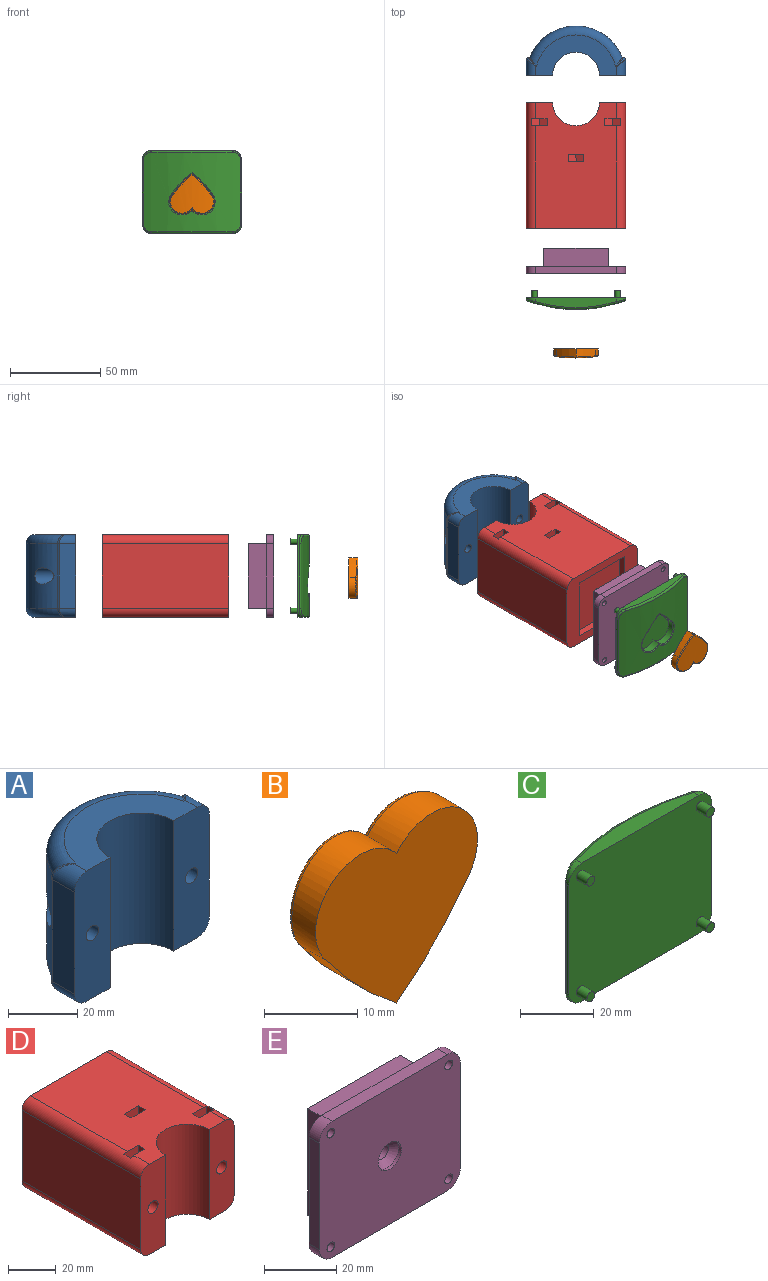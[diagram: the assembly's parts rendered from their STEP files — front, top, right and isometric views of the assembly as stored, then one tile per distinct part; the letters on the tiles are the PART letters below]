
ASSEMBLY  parts=5 mates=4
PART A: 32 faces, bbox 58x29.8x46 mm
  f0: cylinder r=27.5mm len=51.23mm, axis (0,0,-1), area 2176.9mm2, adj f4,f5,f10,f11,f18,f23
  f1: cylinder r=13mm len=46mm, axis (0,0,-1), area 1878.7mm2, adj f2,f7,f8,f9
  f2: plane 46x14.5mm, normal (0,-1,0), area 636.6mm2, adj f1,f3,f8,f9,f14,f16,f21
  f3: plane 36x9mm, normal (1,0,0), area 324mm2, adj f2,f16,f21,f27
  f4: plane 36x0.88mm, normal (0,1,0), area 31.8mm2, adj f0,f17,f22,f27
  f5: plane 36x0.88mm, normal (0,1,0), area 31.8mm2, adj f0,f19,f24,f30
  f6: plane 36x9mm, normal (-1,0,0), area 324mm2, adj f7,f20,f25,f30
  f7: plane 46x14.5mm, normal (0,-1,0), area 636.6mm2, adj f1,f6,f8,f9,f12,f20,f25
  f8: plane 45x22.5mm, normal (0,0,1), area 531.6mm2, adj f1,f2,f7,f21,f22,f23,f24,f25
  f9: plane 45x22.5mm, normal (0,0,-1), area 531.6mm2, adj f1,f2,f7,f16,f17,f18,f19,f20
  f10: cylinder r=4.5mm len=17.54mm, axis (0,-1,0), area 366.3mm2, adj f0,f15
  f11: cylinder r=4.5mm len=17.54mm, axis (0,-1,0), area 366.3mm2, adj f0,f13
  f12: cylinder r=2.5mm len=5mm, axis (0,1,0), area 78.5mm2, adj f7,f13
  f13: plane 9x9mm, normal (0,1,0), area 44mm2, adj f11,f12
  f14: cylinder r=2.5mm len=5mm, axis (0,1,0), area 78.5mm2, adj f2,f15
  f15: plane 9x9mm, normal (0,1,0), area 44mm2, adj f10,f14
  f16: cylinder r=5mm len=9mm, axis (0,1,0), area 59.3mm2, adj f2,f3,f9,f26
  f17: cylinder r=5mm len=5mm, axis (-1,0,0), area 5.7mm2, adj f4,f9,f18,f26
  f18: torus R=22.5mm, axis (0,0,1), area 502.8mm2, adj f0,f9,f17,f19
  f19: cylinder r=5mm len=5mm, axis (-1,0,0), area 5.7mm2, adj f5,f9,f18,f29
  f20: cylinder r=5mm len=9mm, axis (0,-1,0), area 59.3mm2, adj f6,f7,f9,f29
  f21: cylinder r=5mm len=9mm, axis (0,-1,0), area 59.3mm2, adj f2,f3,f8,f28
  f22: cylinder r=5mm len=5mm, axis (1,0,0), area 5.7mm2, adj f4,f8,f23,f28
  f23: torus R=22.5mm, axis (0,0,1), area 502.8mm2, adj f0,f8,f22,f24
  f24: cylinder r=5mm len=5mm, axis (1,0,0), area 5.7mm2, adj f5,f8,f23,f31
  f25: cylinder r=5mm len=9mm, axis (0,1,0), area 59.3mm2, adj f6,f7,f8,f31
  f26: bspline ~5.78x5mm, area 8.5mm2, adj f16,f17,f27
  f27: cylinder r=1mm len=36mm, axis (0,0,-1), area 56.5mm2, adj f3,f4,f26,f28
  f28: bspline ~5.78x5mm, area 8.5mm2, adj f21,f22,f27
  f29: bspline ~5.78x5mm, area 8.5mm2, adj f19,f20,f30
  f30: cylinder r=1mm len=36mm, axis (0,0,-1), area 56.5mm2, adj f5,f6,f29,f31
  f31: bspline ~5.78x5mm, area 8.5mm2, adj f24,f25,f30
PART B: 10 faces, bbox 24.7x5x23.2 mm
  f0: cylinder r=6.89mm len=12.32mm, axis (0,-1,0), area 91.1mm2, adj f1,f3,f4,f9
  f1: cylinder r=6.89mm len=12.32mm, axis (0,-1,0), area 91.1mm2, adj f0,f2,f4,f8
  f2: cylinder r=51.6mm len=10.96mm, axis (0,-1,0), area 65.5mm2, adj f1,f3,f4,f6,f8
  f3: cylinder r=51.6mm len=10.96mm, axis (0,-1,0), area 65.5mm2, adj f0,f2,f4,f7,f9
  f4: plane 24.64x22.3mm, normal (0,-1,0), area 374.5mm2, adj f0,f1,f2,f3
  f5: cylinder r=78.12mm len=23.79mm, axis (0,0,-1), area 330.5mm2, adj f6,f7,f8,f9
  f6: bspline ~14.11x13.57mm, area 11.5mm2, adj f2,f5,f7,f8
  f7: bspline ~14.11x13.57mm, area 11.5mm2, adj f3,f5,f6,f9
  f8: bspline ~13.21x11.89mm, area 16.3mm2, adj f1,f2,f5,f6,f9
  f9: bspline ~13.33x12.41mm, area 16.3mm2, adj f0,f3,f5,f7,f8
PART C: 35 faces, bbox 55x16.9x46 mm
  f0: plane 55x46mm, normal (0,-1,0), area 2480.3mm2, adj f1,f3,f4,f5,f6,f8,f10,f12
  f1: plane 36x0.8mm, normal (1,0,0), area 29mm2, adj f0,f19,f21,f25
  f2: cylinder r=78.12mm len=53.69mm, axis (0,0,-1), area 1973.2mm2, adj f23,f24,f25,f26,f27,f28,f29,f30
  f3: plane 36x0.8mm, normal (-1,0,0), area 29mm2, adj f0,f20,f22,f28
  f4: plane 45x5.5mm, normal (0,0,1), area 197.6mm2, adj f0,f21,f22,f29
  f5: plane 45x5.5mm, normal (0,0,-1), area 197.6mm2, adj f0,f19,f20,f24
  f6: cylinder r=1.5mm len=4mm, axis (0,1,0), area 37.7mm2, adj f0,f7
  f7: plane 3x3mm, normal (0,-1,0), area 7.1mm2, adj f6
  f8: cylinder r=1.5mm len=4mm, axis (0,1,0), area 37.7mm2, adj f0,f9
  f9: plane 3x3mm, normal (0,-1,0), area 7.1mm2, adj f8
  f10: cylinder r=1.5mm len=4mm, axis (0,1,0), area 37.7mm2, adj f0,f11
  f11: plane 3x3mm, normal (0,-1,0), area 7.1mm2, adj f10
  f12: cylinder r=1.5mm len=4mm, axis (0,1,0), area 37.7mm2, adj f0,f13
  f13: plane 3x3mm, normal (0,-1,0), area 7.1mm2, adj f12
  f14: cylinder r=6.89mm len=12.32mm, axis (0,-1,0), area 86mm2, adj f15,f17,f18,f32,f34
  f15: cylinder r=6.89mm len=12.32mm, axis (0,-1,0), area 86mm2, adj f14,f16,f18,f31,f33
  f16: cylinder r=51.6mm len=10.96mm, axis (0,-1,0), area 63mm2, adj f15,f17,f18,f31
  f17: cylinder r=51.6mm len=10.96mm, axis (0,-1,0), area 63mm2, adj f14,f16,f18,f32
  f18: plane 24.64x22.3mm, normal (0,1,0), area 374.5mm2, adj f14,f15,f16,f17
  f19: cylinder r=5mm len=5mm, axis (0,1,0), area 11.6mm2, adj f0,f1,f5,f23
  f20: cylinder r=5mm len=5mm, axis (0,-1,0), area 11.6mm2, adj f0,f3,f5,f26
  f21: cylinder r=5mm len=5mm, axis (0,-1,0), area 11.6mm2, adj f0,f1,f4,f27
  f22: cylinder r=5mm len=5mm, axis (0,1,0), area 11.6mm2, adj f0,f3,f4,f30
  f23: bspline ~6.14x6.08mm, area 10mm2, adj f2,f19,f24,f25
  f24: torus R=77.12mm, axis (0,0,1), area 72.3mm2, adj f2,f5,f23,f26
  f25: cylinder r=1mm len=36mm, axis (0,0,-1), area 43.9mm2, adj f1,f2,f23,f27
  f26: bspline ~6.14x5.29mm, area 10mm2, adj f2,f20,f24,f28
  f27: bspline ~6.14x5.29mm, area 10mm2, adj f2,f21,f25,f29
  f28: cylinder r=1mm len=36mm, axis (0,0,-1), area 43.9mm2, adj f2,f3,f26,f30
  f29: torus R=77.12mm, axis (0,0,1), area 72.3mm2, adj f2,f4,f27,f30
  f30: bspline ~6.14x6.08mm, area 10mm2, adj f2,f22,f28,f29
  f31: bspline ~17.03x16.48mm, area 12.7mm2, adj f2,f15,f16,f32,f33
  f32: bspline ~17.03x16.48mm, area 12.7mm2, adj f2,f14,f17,f31,f34
  f33: bspline ~13.85x13.31mm, area 18.3mm2, adj f2,f15,f31,f34
  f34: bspline ~13.65x12.76mm, area 18.3mm2, adj f2,f14,f32,f33
PART D: 64 faces, bbox 55x70x46 mm
  f0: cylinder r=3mm len=33mm, axis (0,1,0), area 622mm2, adj f31,f36
  f1: plane 55x46mm, normal (0,1,0), area 1212.5mm2, adj f2,f4,f5,f6,f27,f28,f29,f30
  f2: plane 70x45mm, normal (0,0,1), area 2798.5mm2, adj f1,f3,f7,f8,f11,f15,f16,f22
  f3: plane 46x14.5mm, normal (0,-1,0), area 628mm2, adj f2,f5,f6,f8,f10,f41,f42
  f4: plane 70x36mm, normal (-1,0,0), area 2520mm2, adj f1,f7,f40,f43
  f5: plane 70x45mm, normal (0,0,-1), area 2884.5mm2, adj f1,f3,f7,f8,f40,f41
  f6: plane 70x36mm, normal (1,0,0), area 2520mm2, adj f1,f3,f41,f42
  f7: plane 46x14.5mm, normal (0,-1,0), area 628mm2, adj f2,f4,f5,f8,f9,f40,f43
  f8: cylinder r=13mm len=46mm, axis (0,0,-1), area 1878.7mm2, adj f2,f3,f5,f7
  f9: cylinder r=3mm len=9mm, axis (0,-1,0), area 169.6mm2, adj f7,f24
  f10: cylinder r=3mm len=9mm, axis (0,-1,0), area 169.6mm2, adj f3,f16
  f11: plane 25.45x4mm, normal (1,0,0), area 101.8mm2, adj f2,f12,f15,f16
  f12: plane 4.25x4mm, normal (0.5,0,0.87), area 19.6mm2, adj f11,f13,f15,f16
  f13: plane 4.25x4mm, normal (-0.5,0,0.87), area 19.6mm2, adj f12,f14,f15,f16
  f14: plane 25.04x4mm, normal (-1,0,0), area 100.1mm2, adj f13,f15,f16,f42
  f15: plane 27.91x8.5mm, normal (0,-1,0), area 198.2mm2, adj f2,f11,f12,f13,f14,f18,f42
  f16: plane 27.91x8.5mm, normal (0,1,0), area 198.2mm2, adj f2,f10,f11,f12,f13,f14,f42
  f17: cone r=0mm half-angle=59deg, axis (0,-1,0), area 33mm2, adj f18
  f18: cylinder r=3mm len=6mm, axis (0,-1,0), area 37.7mm2, adj f15,f17
  f19: plane 25.04x4mm, normal (1,0,0), area 100.1mm2, adj f20,f23,f24,f43
  f20: plane 4.25x4mm, normal (0.5,0,0.87), area 19.6mm2, adj f19,f21,f23,f24
  f21: plane 4.25x4mm, normal (-0.5,0,0.87), area 19.6mm2, adj f20,f22,f23,f24
  f22: plane 25.45x4mm, normal (-1,0,0), area 101.8mm2, adj f2,f21,f23,f24
  f23: plane 27.91x8.5mm, normal (0,-1,0), area 198.2mm2, adj f2,f19,f20,f21,f22,f26,f43
  f24: plane 27.91x8.5mm, normal (0,1,0), area 198.2mm2, adj f2,f9,f19,f20,f21,f22,f43
  f25: cone r=0mm half-angle=59deg, axis (0,-1,0), area 33mm2, adj f26
  f26: cylinder r=3mm len=6mm, axis (0,-1,0), area 37.7mm2, adj f23,f25
  f27: plane 36x4mm, normal (0,0,1), area 144mm2, adj f1,f28,f30,f31
  f28: plane 36x4mm, normal (-1,0,0), area 144mm2, adj f1,f27,f29,f31
  f29: plane 36x4mm, normal (0,0,-1), area 144mm2, adj f1,f28,f30,f31
  f30: plane 36x4mm, normal (1,0,0), area 144mm2, adj f1,f27,f29,f31
  f31: plane 36x36mm, normal (0,1,0), area 1267.7mm2, adj f0,f27,f28,f29,f30
  f32: plane 25.45x4mm, normal (1,0,0), area 101.8mm2, adj f2,f33,f36,f37
  f33: plane 4.25x4mm, normal (0.5,0,0.87), area 19.6mm2, adj f32,f34,f36,f37
  f34: plane 4.25x4mm, normal (-0.5,0,0.87), area 19.6mm2, adj f33,f35,f36,f37
  f35: plane 25.45x4mm, normal (-1,0,0), area 101.8mm2, adj f2,f34,f36,f37
  f36: plane 27.91x8.5mm, normal (0,-1,0), area 198.5mm2, adj f0,f2,f32,f33,f34,f35
  f37: plane 27.91x8.5mm, normal (0,1,0), area 198.5mm2, adj f2,f32,f33,f34,f35,f39
  f38: cone r=0mm half-angle=59deg, axis (0,1,0), area 33mm2, adj f39
  f39: cylinder r=3mm len=6mm, axis (0,1,0), area 18.8mm2, adj f37,f38
  f40: cylinder r=5mm len=70mm, axis (0,-1,0), area 549.8mm2, adj f1,f4,f5,f7
  f41: cylinder r=5mm len=70mm, axis (0,1,0), area 549.8mm2, adj f1,f3,f5,f6
  f42: cylinder r=5mm len=70mm, axis (0,-1,0), area 541.5mm2, adj f1,f2,f3,f6,f14,f15,f16
  f43: cylinder r=5mm len=70mm, axis (0,1,0), area 541.5mm2, adj f1,f2,f4,f7,f19,f23,f24
  f44: plane 43x5.25mm, normal (0,0,1), area 225.7mm2, adj f45,f51,f52,f53
  f45: cylinder r=5mm len=43mm, axis (0,-1,0), area 337.7mm2, adj f44,f46,f52,f53
  f46: plane 43x28mm, normal (-1,0,0), area 1204mm2, adj f45,f47,f52,f53
  f47: cylinder r=5mm len=43mm, axis (0,-1,0), area 337.7mm2, adj f46,f48,f52,f53
  f48: plane 43x5.25mm, normal (0,0,-1), area 225.7mm2, adj f47,f49,f52,f53
  f49: cylinder r=5mm len=43mm, axis (0,-1,0), area 337.7mm2, adj f48,f50,f52,f53
  f50: plane 43x28mm, normal (1,0,0), area 1204mm2, adj f49,f51,f52,f53
  f51: cylinder r=5mm len=43mm, axis (0,-1,0), area 337.7mm2, adj f44,f50,f52,f53
  f52: plane 38x15.25mm, normal (0,-1,0), area 558mm2, adj f44,f45,f46,f47,f48,f49,f50,f51
  f53: plane 38x15.25mm, normal (0,1,0), area 558mm2, adj f44,f45,f46,f47,f48,f49,f50,f51
  f54: cylinder r=5mm len=43mm, axis (0,-1,0), area 337.7mm2, adj f55,f61,f62,f63
  f55: plane 43x5.25mm, normal (0,0,1), area 225.7mm2, adj f54,f56,f62,f63
  f56: cylinder r=5mm len=43mm, axis (0,-1,0), area 337.7mm2, adj f55,f57,f62,f63
  f57: plane 43x28mm, normal (-1,0,0), area 1204mm2, adj f56,f58,f62,f63
  f58: cylinder r=5mm len=43mm, axis (0,-1,0), area 337.7mm2, adj f57,f59,f62,f63
  f59: plane 43x5.25mm, normal (0,0,-1), area 225.7mm2, adj f58,f60,f62,f63
  f60: cylinder r=5mm len=43mm, axis (0,-1,0), area 337.7mm2, adj f59,f61,f62,f63
  f61: plane 43x28mm, normal (1,0,0), area 1204mm2, adj f54,f60,f62,f63
  f62: plane 38x15.25mm, normal (0,-1,0), area 558mm2, adj f54,f55,f56,f57,f58,f59,f60,f61
  f63: plane 38x15.25mm, normal (0,1,0), area 558mm2, adj f54,f55,f56,f57,f58,f59,f60,f61
PART E: 26 faces, bbox 55x14x46 mm
  f0: plane 36x4mm, normal (-1,0,0), area 144mm2, adj f4,f5,f22,f25
  f1: plane 45x4mm, normal (0,0,-1), area 180mm2, adj f4,f5,f22,f23
  f2: plane 36x4mm, normal (1,0,0), area 144mm2, adj f4,f5,f23,f24
  f3: plane 45x4mm, normal (0,0,1), area 180mm2, adj f4,f5,f24,f25
  f4: plane 55x46mm, normal (0,-1,0), area 2416.6mm2, adj f0,f1,f2,f3,f12,f14,f16,f18
  f5: plane 55x46mm, normal (0,1,0), area 1134mm2, adj f0,f1,f2,f3,f6,f7,f8,f9
  f6: plane 36x10mm, normal (-1,0,0), area 360mm2, adj f5,f7,f9,f10
  f7: plane 36x10mm, normal (0,0,-1), area 360mm2, adj f5,f6,f8,f10
  f8: plane 36x10mm, normal (1,0,0), area 360mm2, adj f5,f7,f9,f10
  f9: plane 36x10mm, normal (0,0,1), area 360mm2, adj f5,f6,f8,f10
  f10: plane 36x36mm, normal (0,1,0), area 1276.4mm2, adj f6,f7,f8,f9,f11
  f11: cylinder r=2.5mm len=11mm, axis (0,-1,0), area 172.8mm2, adj f10,f13
  f12: cylinder r=4.5mm len=9mm, axis (0,-1,0), area 28.3mm2, adj f4,f13
  f13: cone r=2.5mm half-angle=45deg, axis (0,-1,0), area 62.2mm2, adj f11,f12
  f14: cylinder r=1.5mm len=3mm, axis (0,1,0), area 28.3mm2, adj f4,f15
  f15: cone r=1.5mm half-angle=45deg, axis (0,1,0), area 17.8mm2, adj f5,f14
  f16: cylinder r=1.5mm len=3mm, axis (0,1,0), area 28.3mm2, adj f4,f17
  f17: cone r=1.5mm half-angle=45deg, axis (0,1,0), area 17.8mm2, adj f5,f16
  f18: cylinder r=1.5mm len=3mm, axis (0,1,0), area 28.3mm2, adj f4,f19
  f19: cone r=1.5mm half-angle=45deg, axis (0,1,0), area 17.8mm2, adj f5,f18
  f20: cylinder r=1.5mm len=3mm, axis (0,1,0), area 28.3mm2, adj f4,f21
  f21: cone r=1.5mm half-angle=45deg, axis (0,1,0), area 17.8mm2, adj f5,f20
  f22: cylinder r=5mm len=5mm, axis (0,1,0), area 31.4mm2, adj f0,f1,f4,f5
  f23: cylinder r=5mm len=5mm, axis (0,-1,0), area 31.4mm2, adj f1,f2,f4,f5
  f24: cylinder r=5mm len=5mm, axis (0,1,0), area 31.4mm2, adj f2,f3,f4,f5
  f25: cylinder r=5mm len=5mm, axis (0,-1,0), area 31.4mm2, adj f0,f3,f4,f5
PLACE A t=(1.5,61.59,3.04)mm
PLACE B rot(axis=(1,0,0),180deg) t=(1.5,-90.06,3.04)mm
PLACE C rot(axis=(1,0,0),180deg) t=(1.5,-63.18,3.04)mm
PLACE D rot(axis=(0,0,-1),180deg) t=(1.5,46.74,3.04)mm fixed
PLACE E t=(1.5,-44.24,3.04)mm
MATE slider E.f16 <-> C.f8  axis (0,-1,0) through (24.52,-48.24,-16.21)mm
MATE slider C.f18 <-> B.f4  axis (0,-1,0) through (1.5,-63.18,0.01)mm
MATE slider A.f11 <-> D.f10  axis (0,-1,0) through (-18.75,61.59,3.04)mm
MATE slider D.f0 <-> E.f11  axis (0,-1,0) through (1.5,-19.26,3.04)mm
